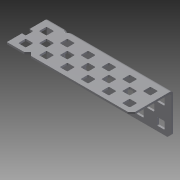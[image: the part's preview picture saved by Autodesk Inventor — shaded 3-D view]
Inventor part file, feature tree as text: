
AUTODESK INVENTOR PART (.ipt)
format: ipt  version: 2014 SP1 (Build 180222100, 222)  size: 877,568 bytes
history: native  units: in
note: dims shown in document units (in); Inventor stores cm internally (conversion verified against a paired STEP export)
features: other x1, imported_body x1, extrude x1, sketch x1
ambient origin geometry x8: Origin, YZ Plane, XZ Plane, XY Plane, X Axis, Y Axis, Z Axis, Center Point
bodies: Body1 (feature_tree)
feature tree (4):
  parser-record x1  (decoder bookkeeping rows leaked as tree rows — omitted from the tree; the rows remain in map.json)
  imported_body  "Base1"
  extrude  "Extrusion1"  Depth=4.5in
  sketch  "Sketch1"  dims[d0=1.0in d1=0.0in d2=4.5in]
